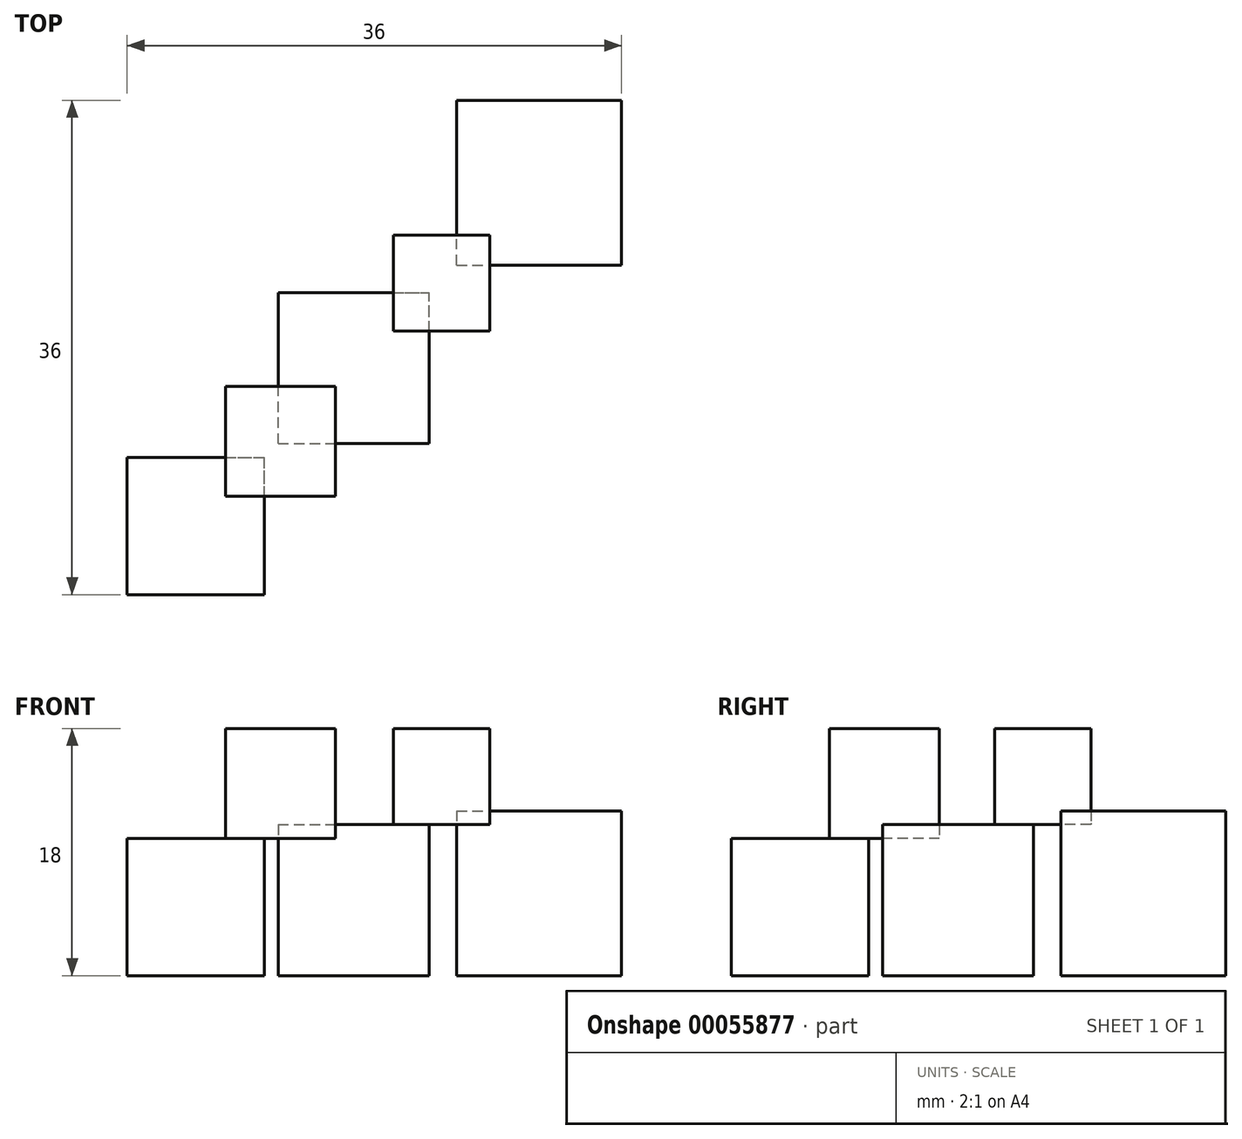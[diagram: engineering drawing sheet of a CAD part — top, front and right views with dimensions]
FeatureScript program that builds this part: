
annotation { "Feature Type Name" : "Feature", "Feature Type Description" : "" }
export const myFeature = defineFeature(function(context is Context, id is Id, definition is map)
    precondition{}
    {
        {
            var Q0;
            Q0=qCreatedBy(makeId("Top.planeOp"),FACE);
            var sketch = newSketch(context, id + "F0", { "sketchPlane" : qUnion([Q0])});
            skLineSegment(sketch, "E0.bottom", {"start": v(0, 0) * mm, "end": v(10, 0) * mm});
            skLineSegment(sketch, "E0.top", {"start": v(0, 10) * mm, "end": v(10, 10) * mm});
            skLineSegment(sketch, "E0.left", {"start": v(0, 0) * mm, "end": v(0, 10) * mm});
            skLineSegment(sketch, "E0.right", {"start": v(10, 0) * mm, "end": v(10, 10) * mm});
            skSolve(sketch);
        }
        {
            var Q0;
            Q0 = qSketchRegion(id + "F0", true);
            extrude(context, id + "F1", {"entities" : qUnion([Q0]), "depth" : 10 * mm});
        }
        {
            var Q0;
            Q0=qCreatedBy(makeId("Top.planeOp"),FACE);
            var sketch = newSketch(context, id + "F2", { "sketchPlane" : qUnion([Q0])});
            skLineSegment(sketch, "E1.bottom", {"start": v(11, 11) * mm, "end": v(22, 11) * mm});
            skLineSegment(sketch, "E1.top", {"start": v(11, 22) * mm, "end": v(22, 22) * mm});
            skLineSegment(sketch, "E1.left", {"start": v(11, 11) * mm, "end": v(11, 22) * mm});
            skLineSegment(sketch, "E1.right", {"start": v(22, 11) * mm, "end": v(22, 22) * mm});
            skSolve(sketch);
        }
        {
            var Q0;
            Q0 = qSketchRegion(id + "F2", true);
            extrude(context, id + "F3", {"entities" : qUnion([Q0]), "depth" : 11 * mm});
        }
        {
            var Q0;
            Q0=qCreatedBy(makeId("Top.planeOp"),FACE);
            var sketch = newSketch(context, id + "F4", { "sketchPlane" : qUnion([Q0])});
            skLineSegment(sketch, "E2.bottom", {"start": v(24, 24) * mm, "end": v(36, 24) * mm});
            skLineSegment(sketch, "E2.top", {"start": v(24, 36) * mm, "end": v(36, 36) * mm});
            skLineSegment(sketch, "E2.left", {"start": v(24, 24) * mm, "end": v(24, 36) * mm});
            skLineSegment(sketch, "E2.right", {"start": v(36, 24) * mm, "end": v(36, 36) * mm});
            skSolve(sketch);
        }
        {
            var Q0;
            Q0 = qSketchRegion(id + "F4", true);
            extrude(context, id + "F5", {"entities" : qUnion([Q0]), "depth" : 12 * mm});
        }
        {
            var Q0;
            Q0=makeQuery(id+"F1.opExtrude","CAP_FACE",FACE,{"disambiguationData":[OSD([sQuery(id+"F0.wireOp",EDGE,"E0.bottom"),sQuery(id+"F0.wireOp",EDGE,"E0.top"),sQuery(id+"F0.wireOp",EDGE,"E0.left"),sQuery(id+"F0.wireOp",EDGE,"E0.right")])],"isStart":false});
            var sketch = newSketch(context, id + "F6", { "sketchPlane" : qUnion([Q0])});
            skLineSegment(sketch, "E3.bottom", {"start": v(7.17, 15.15) * mm, "end": v(15.17, 15.15) * mm});
            skLineSegment(sketch, "E3.top", {"start": v(7.17, 7.15) * mm, "end": v(15.17, 7.15) * mm});
            skLineSegment(sketch, "E3.left", {"start": v(7.17, 15.15) * mm, "end": v(7.17, 7.15) * mm});
            skLineSegment(sketch, "E3.right", {"start": v(15.17, 15.15) * mm, "end": v(15.17, 7.15) * mm});
            skSolve(sketch);
        }
        {
            var Q0;
            Q0 = qSketchRegion(id + "F6", true);
            extrude(context, id + "F7", {"entities" : qUnion([Q0]), "depth" : 8 * mm});
        }
        {
            var Q0;
            Q0=makeQuery(id+"F3.opExtrude","CAP_FACE",FACE,{"disambiguationData":[OSD([sQuery(id+"F2.wireOp",EDGE,"E1.bottom"),sQuery(id+"F2.wireOp",EDGE,"E1.top"),sQuery(id+"F2.wireOp",EDGE,"E1.left"),sQuery(id+"F2.wireOp",EDGE,"E1.right")])],"isStart":false});
            var sketch = newSketch(context, id + "F8", { "sketchPlane" : qUnion([Q0])});
            skLineSegment(sketch, "E4.bottom", {"start": v(19.4, 26.19) * mm, "end": v(26.4, 26.19) * mm});
            skLineSegment(sketch, "E4.top", {"start": v(19.4, 19.19) * mm, "end": v(26.4, 19.19) * mm});
            skLineSegment(sketch, "E4.left", {"start": v(19.4, 26.19) * mm, "end": v(19.4, 19.19) * mm});
            skLineSegment(sketch, "E4.right", {"start": v(26.4, 26.19) * mm, "end": v(26.4, 19.19) * mm});
            skSolve(sketch);
        }
        {
            var Q0;
            Q0 = qSketchRegion(id + "F8", true);
            extrude(context, id + "F9", {"entities" : qUnion([Q0]), "depth" : 7 * mm});
        }
    });
